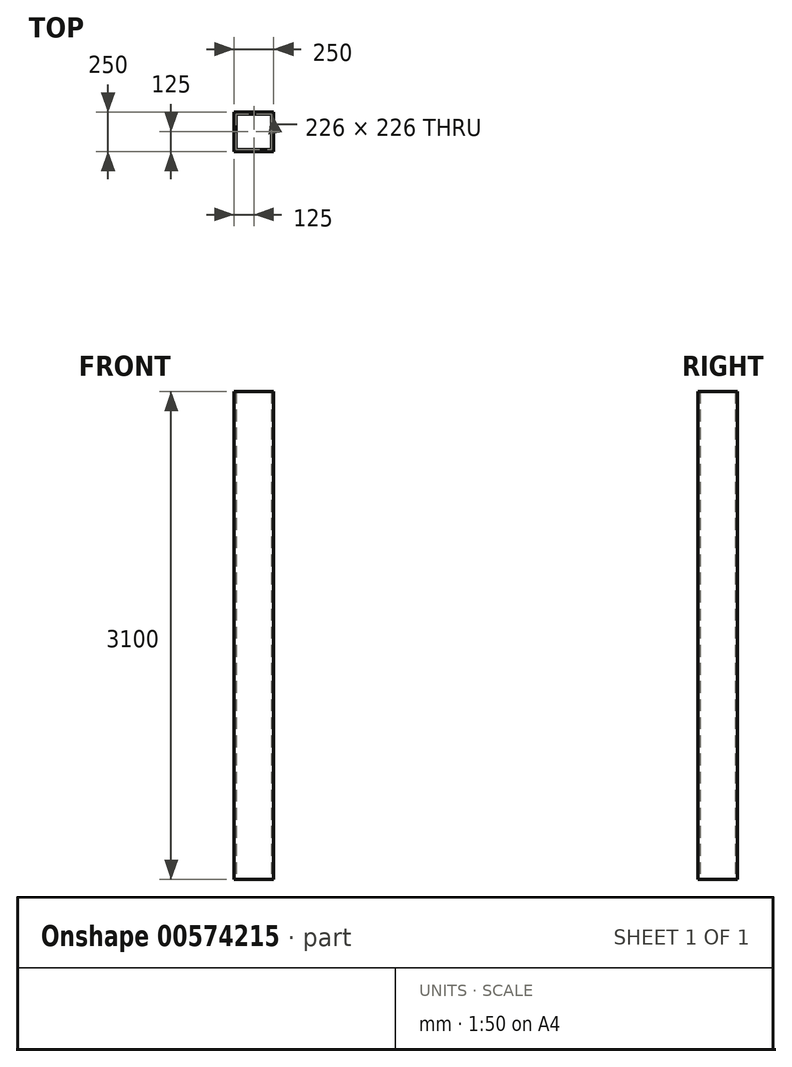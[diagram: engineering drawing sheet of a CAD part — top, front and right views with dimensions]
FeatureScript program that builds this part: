
annotation { "Feature Type Name" : "Feature", "Feature Type Description" : "" }
export const myFeature = defineFeature(function(context is Context, id is Id, definition is map)
    precondition{}
    {
        {
            var Q0;
            Q0=qCreatedBy(makeId("Top.planeOp"),FACE);
            var sketch = newSketch(context, id + "F0", { "sketchPlane" : qUnion([Q0])});
            skLineSegment(sketch, "E0.bottom", {"start": v(0, 0) * mm, "end": v(250, 0) * mm});
            skLineSegment(sketch, "E0.top", {"start": v(0, 250) * mm, "end": v(250, 250) * mm});
            skLineSegment(sketch, "E0.left", {"start": v(0, 0) * mm, "end": v(0, 250) * mm});
            skLineSegment(sketch, "E0.right", {"start": v(250, 0) * mm, "end": v(250, 250) * mm});
            skLineSegment(sketch, "E1.0", {"start": v(12, 12) * mm, "end": v(238, 12) * mm});
            skLineSegment(sketch, "E1.1", {"start": v(12, 12) * mm, "end": v(12, 238) * mm});
            skLineSegment(sketch, "E1.2", {"start": v(12, 238) * mm, "end": v(238, 238) * mm});
            skLineSegment(sketch, "E1.3", {"start": v(238, 12) * mm, "end": v(238, 238) * mm});
            skSolve(sketch);
        }
        {
            var Q0;
            Q0 = qSketchRegion(id + "F0", true);
            extrude(context, id + "F1", {"entities" : qUnion([Q0]), "depth" : 3100 * mm, "offsetDistance" : 25 * mm});
        }
    });
